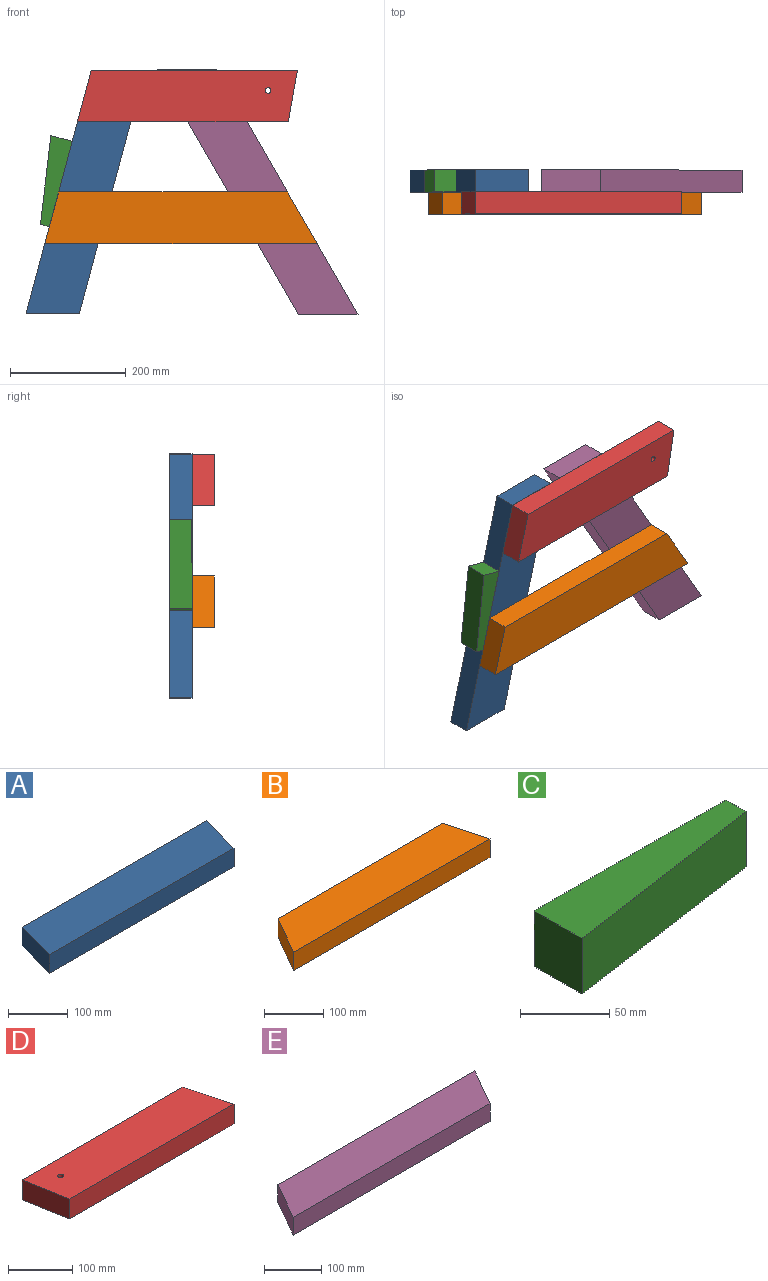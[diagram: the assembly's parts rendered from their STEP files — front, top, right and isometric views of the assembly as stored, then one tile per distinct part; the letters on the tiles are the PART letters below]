
ASSEMBLY  parts=5 mates=4
PART A: 6 faces, bbox 458.8x88.9x38.1 mm
  f0: plane 434.97x38.1mm, normal (0,1,0), area 16572.2mm2, adj f1,f3,f4,f5
  f1: plane 88.9x38.1mm, normal (-0.97,0.26,0), area 3506.6mm2, adj f0,f2,f4,f5
  f2: plane 434.97x38.1mm, normal (0,-1,0), area 16572.2mm2, adj f1,f3,f4,f5
  f3: plane 88.9x38.1mm, normal (0.97,-0.26,0), area 3506.6mm2, adj f0,f2,f4,f5
  f4: plane 458.79x88.9mm, normal (0,0,1), area 38668.5mm2, adj f0,f1,f2,f3
  f5: plane 458.79x88.9mm, normal (0,0,-1), area 38668.5mm2, adj f0,f1,f2,f3
PART B: 6 faces, bbox 469.9x88.9x38.1 mm
  f0: plane 88.9x38.1mm, normal (0.97,0.26,0), area 3506.6mm2, adj f1,f3,f4,f5
  f1: plane 394.75x38.1mm, normal (0,1,0), area 15040.1mm2, adj f0,f2,f4,f5
  f2: plane 88.9x51.33mm, normal (-0.87,0.5,0), area 3911.1mm2, adj f1,f3,f4,f5
  f3: plane 469.9x38.1mm, normal (0,-1,0), area 17903.2mm2, adj f0,f2,f4,f5
  f4: plane 469.9x88.9mm, normal (0,0,1), area 38433.8mm2, adj f0,f1,f2,f3
  f5: plane 469.9x88.9mm, normal (0,0,-1), area 38433.8mm2, adj f0,f1,f2,f3
PART C: 6 faces, bbox 152.4x38.1x38.1 mm
  f0: plane 152.4x38.1mm, normal (0,1,0), area 5806.4mm2, adj f1,f3,f4,f5
  f1: plane 38.1x38.1mm, normal (-1,0,0), area 1451.6mm2, adj f0,f2,f4,f5
  f2: plane 152.4x38.1mm, normal (0.14,-0.99,0), area 5867.9mm2, adj f1,f3,f4,f5
  f3: plane 38.1x15.88mm, normal (1,0,0), area 604.8mm2, adj f0,f2,f4,f5
  f4: plane 152.4x38.1mm, normal (0,0,1), area 4112.9mm2, adj f0,f1,f2,f3
  f5: plane 152.4x38.1mm, normal (0,0,-1), area 4112.9mm2, adj f0,f1,f2,f3
PART D: 7 faces, bbox 379.4x88.9x38.1 mm
  f0: plane 355.59x38.1mm, normal (0,1,0), area 13548mm2, adj f1,f4,f5,f6
  f1: plane 88.9x38.1mm, normal (-0.98,-0.17,0), area 3439.3mm2, adj f0,f2,f5,f6
  f2: plane 363.74x38.1mm, normal (0,-1,0), area 13858.4mm2, adj f1,f4,f5,f6
  f3: cylinder r=4.76mm len=38.1mm, axis (0,0,-1), area 1140.1mm2, adj f5,f6
  f4: plane 88.9x38.1mm, normal (0.97,0.26,0), area 3506.6mm2, adj f0,f2,f5,f6
  f5: plane 379.41x88.9mm, normal (0,0,1), area 31902.9mm2, adj f0,f1,f2,f3,f4
  f6: plane 379.41x88.9mm, normal (0,0,-1), area 31902.9mm2, adj f0,f1,f2,f3,f4
PART E: 6 faces, bbox 538.2x88.9x38.1 mm
  f0: plane 486.84x38.1mm, normal (0,1,0), area 18548.5mm2, adj f1,f3,f4,f5
  f1: plane 88.9x51.33mm, normal (-0.87,0.5,0), area 3911.1mm2, adj f0,f2,f4,f5
  f2: plane 486.84x38.1mm, normal (0,-1,0), area 18548.5mm2, adj f1,f3,f4,f5
  f3: plane 88.9x51.33mm, normal (0.87,-0.5,0), area 3911.1mm2, adj f0,f2,f4,f5
  f4: plane 538.16x88.9mm, normal (0,0,1), area 43279.7mm2, adj f0,f1,f2,f3
  f5: plane 538.16x88.9mm, normal (0,0,-1), area 43279.7mm2, adj f0,f1,f2,f3
PLACE A rot(axis=(-0.68,-0.52,-0.52),111.8deg) t=(-419.12,-19.05,210.81)mm
PLACE B rot(axis=(0,-0.71,-0.71),180deg) t=(-279.67,-57.15,166.36)mm
PLACE C rot(axis=(0.48,0.62,-0.62),129deg) t=(-461.44,19.05,224.6)mm
PLACE D rot(axis=(0,-0.71,-0.71),180deg) t=(-238.89,-57.15,376.43)mm
PLACE E rot(axis=(0.38,-0.65,0.65),138.6deg) t=(-121.71,19.05,210.81)mm fixed
MATE fastened B.f0 <-> A.f2  axis (-0.97,0,0.26) through (-465.14,-19.05,210.81)mm
MATE fastened A.f2 <-> C.f0  axis (-0.97,0,0.26) through (-408.85,19.05,420.88)mm
MATE fastened A.f2 <-> D.f4  axis (-0.97,0,0.26) through (-408.85,-19.05,420.88)mm
MATE fastened B.f2 <-> E.f2  axis (0.87,0,0.5) through (-70.38,-19.05,210.81)mm
